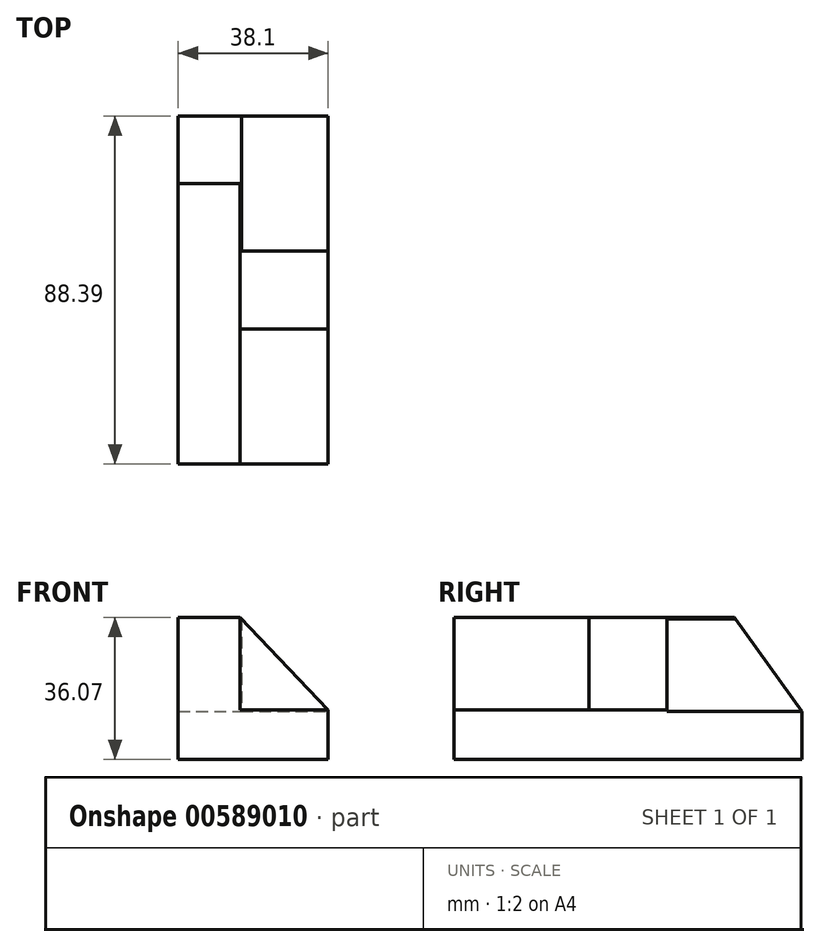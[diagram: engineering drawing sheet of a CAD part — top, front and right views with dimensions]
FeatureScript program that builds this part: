
annotation { "Feature Type Name" : "Feature", "Feature Type Description" : "" }
export const myFeature = defineFeature(function(context is Context, id is Id, definition is map)
    precondition{}
    {
        {
            var Q0;
            Q0=qCreatedBy(makeId("Front.planeOp"),FACE);
            var sketch = newSketch(context, id + "F0", { "sketchPlane" : qUnion([Q0])});
            skLineSegment(sketch, "E0", {"start": v(-72.64, 0) * mm, "end": v(-72.64, 36.07) * mm});
            skLineSegment(sketch, "E1", {"start": v(-72.64, 36.07) * mm, "end": v(-9.14, 36.07) * mm});
            skLineSegment(sketch, "E2", {"start": v(-9.14, 36.07) * mm, "end": v(-9.14, 0) * mm});
            skLineSegment(sketch, "E3", {"start": v(-9.14, 0) * mm, "end": v(-72.64, 0) * mm});
            skSolve(sketch);
        }
        {
            var Q0;
            Q0=makeQuery(id+"F0.imprint","IMPRINT",FACE,{"disambiguationData":[TD([[makeQuery(id+"F0.imprint","IMPRINT",EDGE,{"derivedFrom":sQuery(id+"F0.wireOp",EDGE,"E0")}),-1.0]])]});
            extrude(context, id + "F1", {"entities" : qUnion([Q0]), "depth" : 25.4 * mm, "offsetDistance" : 25.4 * mm});
        }
        {
            var Q0;
            Q0=makeQuery(id+"F1.opExtrude","CAP_FACE",FACE,{"disambiguationData":[OSD([sQuery(id+"F0.wireOp",EDGE,"E0"),sQuery(id+"F0.wireOp",EDGE,"E1"),sQuery(id+"F0.wireOp",EDGE,"E2"),sQuery(id+"F0.wireOp",EDGE,"E3")])],"isStart":true});
            extrude(context, id + "F2", {"entities" : qUnion([Q0]), "operationType" : NewBodyOperationType.ADD, "depth" : 63 * mm, "offsetDistance" : 25.4 * mm});
        }
        {
            var Q0;
            Q0=makeQuery(id+"F2.opExtrude","CAP_FACE",FACE,{"disambiguationData":[OSD([sQuery(id+"F0.wireOp",EDGE,"E0"),sQuery(id+"F0.wireOp",EDGE,"E1"),sQuery(id+"F0.wireOp",EDGE,"E2"),sQuery(id+"F0.wireOp",EDGE,"E3")])],"isStart":false});
            var sketch = newSketch(context, id + "F3", { "sketchPlane" : qUnion([Q0])});
            skLineSegment(sketch, "E4", {"start": v(56.6, 36.07) * mm, "end": v(56.6, 12.25) * mm});
            skLineSegment(sketch, "E5", {"start": v(56.6, 12.25) * mm, "end": v(9.14, 12.25) * mm});
            skSolve(sketch);
        }
        {
            var Q0;
            Q0=makeQuery(id+"F1.opExtrude","CAP_FACE",FACE,{"disambiguationData":[OSD([sQuery(id+"F0.wireOp",EDGE,"E0"),sQuery(id+"F0.wireOp",EDGE,"E1"),sQuery(id+"F0.wireOp",EDGE,"E2"),sQuery(id+"F0.wireOp",EDGE,"E3")])],"isStart":false});
            var sketch = newSketch(context, id + "F4", { "sketchPlane" : qUnion([Q0])});
            skLineSegment(sketch, "E6", {"start": v(-56.9, 36.07) * mm, "end": v(-56.9, 12.56) * mm});
            skLineSegment(sketch, "E7", {"start": v(-56.9, 12.56) * mm, "end": v(-9.14, 12.56) * mm});
            skSolve(sketch);
        }
        {
            var Q0;
            {var subQ0=sQuery(id+"F4.wireOp",EDGE,"E6");Q0=makeQuery(id+"F4.imprint","IMPRINT",FACE,{"disambiguationData":[TD([[makeQuery(id+"F4.imprint","IMPRINT",EDGE,{"derivedFrom":subQ0}),1.0]])]});}
            extrude(context, id + "F5", {"entities" : qUnion([Q0]), "operationType" : NewBodyOperationType.REMOVE, "oppositeDirection" : true, "depth" : 34.3 * mm, "offsetDistance" : 25.4 * mm});
        }
        {
            var Q0;
            {var subQ0=sQuery(id+"F3.wireOp",EDGE,"E4");Q0=makeQuery(id+"F3.imprint","IMPRINT",FACE,{"disambiguationData":[TD([[makeQuery(id+"F3.imprint","IMPRINT",EDGE,{"derivedFrom":subQ0}),-1.0]])]});}
            extrude(context, id + "F6", {"entities" : qUnion([Q0]), "operationType" : NewBodyOperationType.REMOVE, "oppositeDirection" : true, "depth" : 34.3 * mm, "offsetDistance" : 25.4 * mm});
        }
        {
            var Q0;
            Q0=makeQuery(id+"F6.boolean.opBoolean","COPY",FACE,{"derivedFrom":makeQuery(id+"F6.opExtrude","SWEPT_FACE",FACE,{"disambiguationData":[OSD([sQuery(id+"F3.wireOp",EDGE,"E4")])]})});
            var sketch = newSketch(context, id + "F7", { "sketchPlane" : qUnion([Q0])});
            skLineSegment(sketch, "E8", {"start": v(45.85, 36.07) * mm, "end": v(63, 12.25) * mm});
            skSolve(sketch);
        }
        {
            var Q0;
            {var subQ0=sQuery(id+"F0.wireOp",EDGE,"E2");Q0=makeQuery(id+"F2.boolean.opBoolean","MERGE",FACE,{"derivedFrom":[makeQuery(id+"F1.opExtrude","SWEPT_FACE",FACE,{"disambiguationData":[OSD([subQ0])]}),makeQuery(id+"F2.opExtrude","SWEPT_FACE",FACE,{"disambiguationData":[OSD([subQ0])]})]});}
            extrude(context, id + "F8", {"entities" : qUnion([Q0]), "operationType" : NewBodyOperationType.REMOVE, "oppositeDirection" : true, "depth" : 25.4 * mm, "offsetDistance" : 25.4 * mm});
        }
        {
            var Q0;
            {var subQ0=sQuery(id+"F7.wireOp",EDGE,"E8");Q0=makeQuery(id+"F7.imprint","IMPRINT",FACE,{"disambiguationData":[TD([[makeQuery(id+"F7.imprint","IMPRINT",EDGE,{"derivedFrom":subQ0}),1.0]])]});}
            extrude(context, id + "F9", {"entities" : qUnion([Q0]), "operationType" : NewBodyOperationType.REMOVE, "oppositeDirection" : true, "depth" : 25.4 * mm, "offsetDistance" : 25.4 * mm});
        }
        {
            var Q0;
            Q0=makeQuery(id+"F5.boolean.opBoolean","COPY",FACE,{"derivedFrom":makeQuery(id+"F5.opExtrude","CAP_FACE",FACE,{"disambiguationData":[OSD([sQuery(id+"F0.wireOp",EDGE,"E1"),sQuery(id+"F0.wireOp",EDGE,"E2"),sQuery(id+"F4.wireOp",EDGE,"E6"),sQuery(id+"F4.wireOp",EDGE,"E7")])],"isStart":false})});
            var sketch = newSketch(context, id + "F10", { "sketchPlane" : qUnion([Q0])});
            skLineSegment(sketch, "E9", {"start": v(-56.9, 36.07) * mm, "end": v(-34.54, 12.56) * mm});
            skSolve(sketch);
        }
        {
            var Q0;
            Q0=makeQuery(id+"F10.imprint","IMPRINT",FACE,{"disambiguationData":[TD([[makeQuery(id+"F10.imprint","IMPRINT",EDGE,{"derivedFrom":sQuery(id+"F10.wireOp",EDGE,"E9")}),1.0]])]});
            extrude(context, id + "F11", {"entities" : qUnion([Q0]), "operationType" : NewBodyOperationType.REMOVE, "oppositeDirection" : true, "depth" : 41.4 * mm, "offsetDistance" : 25.4 * mm});
        }
    });
